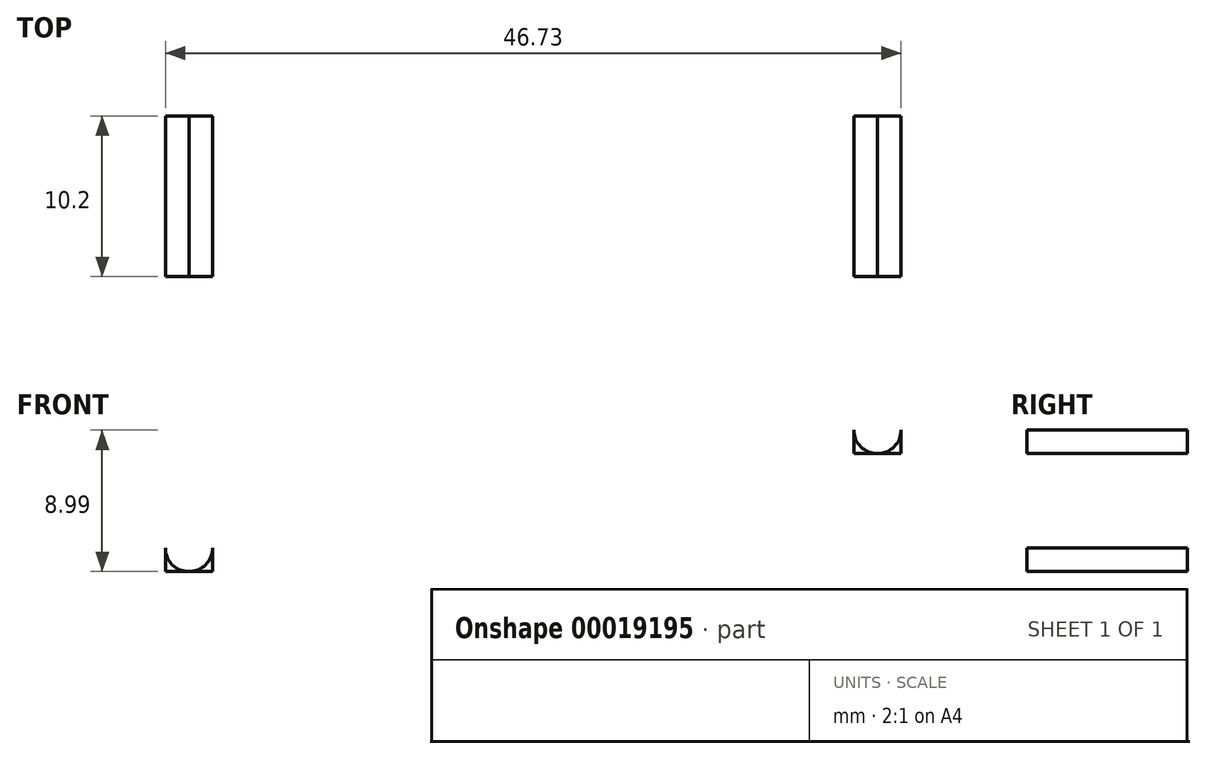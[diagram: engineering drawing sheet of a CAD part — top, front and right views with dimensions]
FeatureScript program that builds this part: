
annotation { "Feature Type Name" : "Feature", "Feature Type Description" : "" }
export const myFeature = defineFeature(function(context is Context, id is Id, definition is map)
    precondition{}
    {
        {
            var Q0;
            Q0=qCreatedBy(makeId("Front.planeOp"),FACE);
            var sketch = newSketch(context, id + "F0", { "sketchPlane" : qUnion([Q0])});
            skLineSegment(sketch, "E0.rect.bottom", {"start": v(1.5, 7.5) * mm, "end": v(-1.5, 7.5) * mm, "construction": true});
            skLineSegment(sketch, "E0.rect.top", {"start": v(1.5, -7.5) * mm, "end": v(-1.5, -7.5) * mm});
            skLineSegment(sketch, "E0.rect.left", {"start": v(1.5, 7.5) * mm, "end": v(1.5, -7.5) * mm});
            skLineSegment(sketch, "E0.rect.right", {"start": v(-1.5, 7.5) * mm, "end": v(-1.5, -7.5) * mm});
            skPoint(sketch, "E0.rect.middle", {"position": v(0, 0) * mm});
            skLineSegment(sketch, "E1.rect.bottom", {"start": v(45.23, 0) * mm, "end": v(42.23, 0) * mm});
            skLineSegment(sketch, "E1.rect.top", {"start": v(45.23, 3.3) * mm, "end": v(42.23, 3.3) * mm, "construction": true});
            skLineSegment(sketch, "E1.rect.left", {"start": v(45.23, 0) * mm, "end": v(45.23, 3.3) * mm});
            skLineSegment(sketch, "E1.rect.right", {"start": v(42.23, 0) * mm, "end": v(42.23, 3.3) * mm});
            skPoint(sketch, "E1.rect.middle", {"position": v(43.73, 1.65) * mm});
            skArc(sketch, "E2", {"start": v(-1.5, -6) * mm, "mid": v(0, -7.5) * mm, "end": v(1.5, -6) * mm});
            skArc(sketch, "E3", {"start": v(42.23, 1.5) * mm, "mid": v(43.73, 0) * mm, "end": v(45.23, 1.5) * mm});
            skSolve(sketch);
        }
        {
            var Q0;
            {var subQ1=sQuery(id+"F0.wireOp",EDGE,"E0.rect.top");var subQ3=sQuery(id+"F0.wireOp",EDGE,"E0.rect.left");var subQ5=makeQuery(id+"F0.imprint","INTERSECT",VERTEX,{"derivedFrom":[subQ1,subQ3]});Q0=makeQuery(id+"F0.imprint","IMPRINT",FACE,{"disambiguationData":[TD([[makeQuery(id+"F0.imprint","IMPRINT",EDGE,{"disambiguationData":[TD([[subQ5,-1.0]])],"derivedFrom":subQ1}),-1.0]])]});}
            var Q1;
            {var subQ1=sQuery(id+"F0.wireOp",EDGE,"E0.rect.top");var subQ3=sQuery(id+"F0.wireOp",EDGE,"E0.rect.right");var subQ5=makeQuery(id+"F0.imprint","INTERSECT",VERTEX,{"derivedFrom":[subQ1,subQ3]});Q1=makeQuery(id+"F0.imprint","IMPRINT",FACE,{"disambiguationData":[TD([[makeQuery(id+"F0.imprint","IMPRINT",EDGE,{"disambiguationData":[TD([[subQ5,1.0]])],"derivedFrom":subQ1}),-1.0]])]});}
            var Q2;
            {var subQ1=sQuery(id+"F0.wireOp",EDGE,"E1.rect.bottom");var subQ3=sQuery(id+"F0.wireOp",EDGE,"E1.rect.left");var subQ5=makeQuery(id+"F0.imprint","INTERSECT",VERTEX,{"derivedFrom":[subQ1,subQ3]});Q2=makeQuery(id+"F0.imprint","IMPRINT",FACE,{"disambiguationData":[TD([[makeQuery(id+"F0.imprint","IMPRINT",EDGE,{"disambiguationData":[TD([[subQ5,-1.0]])],"derivedFrom":subQ1}),-1.0]])]});}
            var Q3;
            {var subQ1=sQuery(id+"F0.wireOp",EDGE,"E1.rect.bottom");var subQ3=sQuery(id+"F0.wireOp",EDGE,"E1.rect.right");var subQ5=makeQuery(id+"F0.imprint","INTERSECT",VERTEX,{"derivedFrom":[subQ1,subQ3]});Q3=makeQuery(id+"F0.imprint","IMPRINT",FACE,{"disambiguationData":[TD([[makeQuery(id+"F0.imprint","IMPRINT",EDGE,{"disambiguationData":[TD([[subQ5,1.0]])],"derivedFrom":subQ1}),-1.0]])]});}
            extrude(context, id + "F1", {"entities" : qUnion([Q0, Q1, Q2, Q3]), "depth" : 10.2 * mm});
        }
    });
